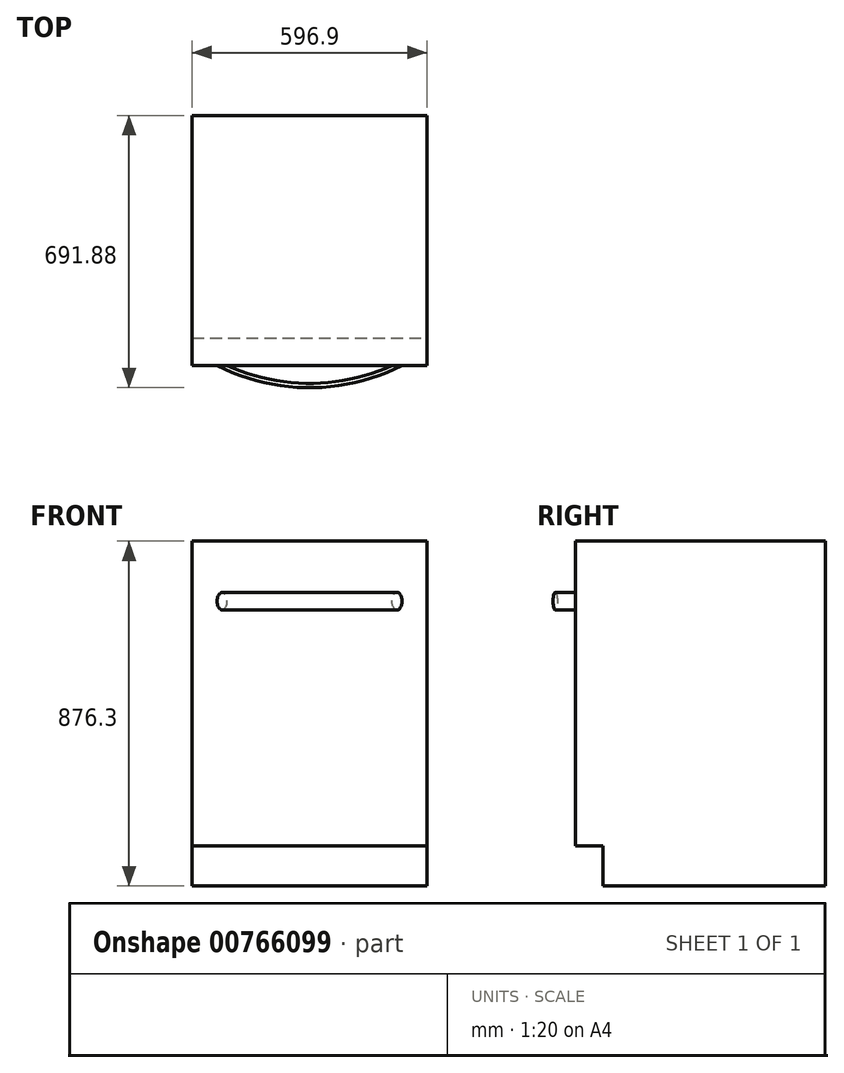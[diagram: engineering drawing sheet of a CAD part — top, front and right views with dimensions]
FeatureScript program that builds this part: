
annotation { "Feature Type Name" : "Feature", "Feature Type Description" : "" }
export const myFeature = defineFeature(function(context is Context, id is Id, definition is map)
    precondition{}
    {
        {
            var Q0;
            Q0=qCreatedBy(makeId("Top.planeOp"),FACE);
            var sketch = newSketch(context, id + "F0", { "sketchPlane" : qUnion([Q0])});
            skLineSegment(sketch, "E0.bottom", {"start": v(298.45, -317.5) * mm, "end": v(-298.45, -317.5) * mm});
            skLineSegment(sketch, "E0.top", {"start": v(298.45, 317.5) * mm, "end": v(-298.45, 317.5) * mm});
            skLineSegment(sketch, "E0.left", {"start": v(298.45, -317.5) * mm, "end": v(298.45, 317.5) * mm});
            skLineSegment(sketch, "E0.right", {"start": v(-298.45, -317.5) * mm, "end": v(-298.45, 317.5) * mm});
            skPoint(sketch, "E0.middle", {"position": v(0, 0) * mm});
            skSolve(sketch);
        }
        {
            var Q0;
            Q0=makeQuery(id+"F0.imprint","IMPRINT",FACE,{"disambiguationData":[TD([[makeQuery(id+"F0.imprint","IMPRINT",EDGE,{"derivedFrom":sQuery(id+"F0.wireOp",EDGE,"E0.bottom")}),-1.0]])]});
            extrude(context, id + "F1", {"entities" : qUnion([Q0]), "oppositeDirection" : true, "depth" : 876.3 * mm, "offsetDistance" : 25.4 * mm});
        }
        {
            var Q0;
            Q0=makeQuery(id+"F1.opExtrude","CAP_FACE",FACE,{"disambiguationData":[OSD([sQuery(id+"F0.wireOp",EDGE,"E0.bottom"),sQuery(id+"F0.wireOp",EDGE,"E0.top"),sQuery(id+"F0.wireOp",EDGE,"E0.left"),sQuery(id+"F0.wireOp",EDGE,"E0.right")])],"isStart":true});
            cPlane(context, id + "F2", {"entities" : qUnion([Q0]), "cplaneType" : CPlaneType.OFFSET, "offset" : 152.4 * mm, "oppositeDirection" : true, "width" : 152.4 * mm, "height" : 152.4 * mm});
        }
        {
            var Q0;
            Q0=qCreatedBy(id+"F2.planeOp",FACE);
            var sketch = newSketch(context, id + "F3", { "sketchPlane" : qUnion([Q0])});
            skPoint(sketch, "E1.0", {"position": v(0, -317.5) * mm});
            skLineSegment(sketch, "E2.0", {"start": v(298.45, -317.5) * mm, "end": v(-298.45, -317.5) * mm});
            skArc(sketch, "E3", {"start": v(-222.25, -317.5) * mm, "mid": v(23.63, -368.15) * mm, "end": v(263.74, -294.87) * mm});
            skPoint(sketch, "E4.orphan", {"position": v(222.25, -317.5) * mm});
            skSolve(sketch);
        }
        {
            var Q0;
            Q0=makeQuery(id+"F1.opExtrude","SWEPT_FACE",FACE,{"disambiguationData":[OSD([sQuery(id+"F0.wireOp",EDGE,"E0.bottom")])]});
            var sketch = newSketch(context, id + "F4", { "sketchPlane" : qUnion([Q0])});
            skPoint(sketch, "E5.0", {"position": v(-222.25, -152.4) * mm});
            skEllipse(sketch, "E6", {"center": v(-222.25, -152.4) * mm, "majorRadius": 22.23 * mm, "minorRadius": 12.7 * mm, "majorAxis": v(0, 1)});
            skSolve(sketch);
        }
        {
            var Q0;
            Q0=makeQuery(id+"F4.imprint","IMPRINT",FACE,{"disambiguationData":[TD([[makeQuery(id+"F4.imprint","IMPRINT",EDGE,{"derivedFrom":sQuery(id+"F4.wireOp",EDGE,"E6")}),1.0]])]});
            var Q1;
            Q1=sQuery(id+"F3.wireOp",EDGE,"E3");
            sweep(context, id + "F5", {"operationType" : NewBodyOperationType.ADD, "profiles" : qUnion([Q0]), "path" : qUnion([Q1])});
        }
        {
            var Q0;
            Q0=makeQuery(id+"F1.opExtrude","SWEPT_FACE",FACE,{"disambiguationData":[OSD([sQuery(id+"F0.wireOp",EDGE,"E0.left")])]});
            var sketch = newSketch(context, id + "F6", { "sketchPlane" : qUnion([Q0])});
            skLineSegment(sketch, "E7.bottom", {"start": v(-317.5, -876.3) * mm, "end": v(-247.65, -876.3) * mm});
            skLineSegment(sketch, "E7.top", {"start": v(-317.5, -774.7) * mm, "end": v(-247.65, -774.7) * mm});
            skLineSegment(sketch, "E7.left", {"start": v(-317.5, -876.3) * mm, "end": v(-317.5, -774.7) * mm});
            skLineSegment(sketch, "E7.right", {"start": v(-247.65, -876.3) * mm, "end": v(-247.65, -774.7) * mm});
            skSolve(sketch);
        }
        {
            var Q0;
            Q0=makeQuery(id+"F6.imprint","IMPRINT",FACE,{"disambiguationData":[TD([[makeQuery(id+"F6.imprint","IMPRINT",EDGE,{"derivedFrom":sQuery(id+"F6.wireOp",EDGE,"E7.bottom")}),1.0]])]});
            extrude(context, id + "F7", {"entities" : qUnion([Q0]), "operationType" : NewBodyOperationType.REMOVE, "endBound" : BoundingType.THROUGH_ALL, "oppositeDirection" : true, "depth" : 25.4 * mm, "offsetDistance" : 25.4 * mm});
        }
    });
